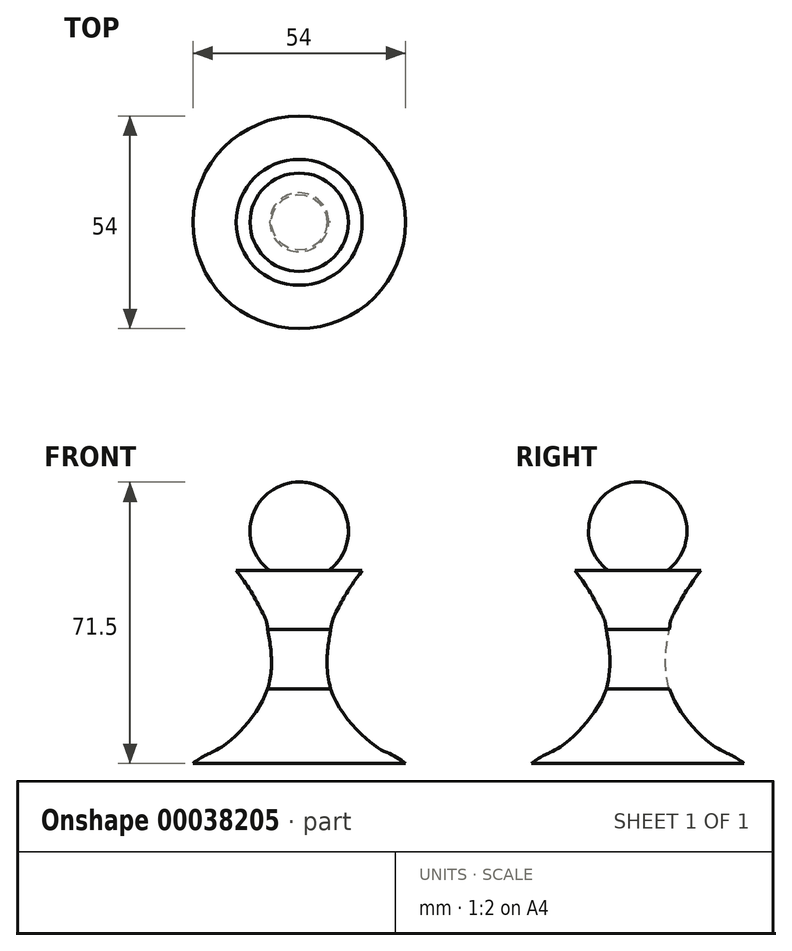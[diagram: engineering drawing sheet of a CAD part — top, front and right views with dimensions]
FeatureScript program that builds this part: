
annotation { "Feature Type Name" : "Feature", "Feature Type Description" : "" }
export const myFeature = defineFeature(function(context is Context, id is Id, definition is map)
    precondition{}
    {
        {
            var Q0;
            Q0=qCreatedBy(makeId("Front.planeOp"),FACE);
            var sketch = newSketch(context, id + "F0", { "sketchPlane" : qUnion([Q0])});
            skArc(sketch, "E0", {"start": v(7.5, 17) * mm, "mid": v(11.86, 30.95) * mm, "end": v(0, 39.5) * mm});
            skLineSegment(sketch, "E1", {"start": v(0, 27) * mm, "end": v(0, 17) * mm});
            skLineSegment(sketch, "E2", {"start": v(7.5, 17) * mm, "end": v(16, 17) * mm});
            skLineSegment(sketch, "E3", {"start": v(16, 17) * mm, "end": v(7.5, 17) * mm});
            skLineSegment(sketch, "E4", {"start": v(0, 17) * mm, "end": v(0, 2) * mm});
            skLineSegment(sketch, "E5", {"start": v(8, 2) * mm, "end": v(8, -13) * mm});
            skLineSegment(sketch, "E6", {"start": v(0, -13) * mm, "end": v(0, -28) * mm});
            skLineSegment(sketch, "E7", {"start": v(0, -32) * mm, "end": v(27, -32) * mm});
            skLineSegment(sketch, "E8", {"start": v(27, -32) * mm, "end": v(0, -32) * mm});
            skLineSegment(sketch, "E9", {"start": v(0, -30) * mm, "end": v(0, -32) * mm});
            skLineSegment(sketch, "E10", {"start": v(0, -30) * mm, "end": v(0, -28) * mm});
            skFitSpline(sketch, "E11", {"points": [v(16, 17) * mm, v(12.1, 11.43) * mm, v(10.8, 9.2) * mm, v(9.27, 6.27) * mm, v(8.37, 4.17) * mm, v(8, 2) * mm, v(8, -13) * mm, v(20, -28) * mm, v(24, -30) * mm, v(27, -32) * mm], "startDerivative": vector(-41.3, -51.96) * mm, "endDerivative": vector(25.72, -19.41) * mm});
            skLineSegment(sketch, "E12", {"start": v(0, 27) * mm, "end": v(0, 39.5) * mm});
            skLineSegment(sketch, "E13", {"start": v(0, 2) * mm, "end": v(0, -13) * mm});
            skSolve(sketch);
        }
        {
            var Q0;
            Q0=makeQuery(id+"F0.imprint","IMPRINT",FACE,{"disambiguationData":[TD([[makeQuery(id+"F0.imprint","IMPRINT",EDGE,{"derivedFrom":sQuery(id+"F0.wireOp",EDGE,"E0")}),1.0]])]});
            var Q1;
            Q1=sQuery(id+"F0.wireOp",EDGE,"E4");
            revolve(context, id + "F1", {"entities" : qUnion([Q0]), "axis" : qUnion([Q1]), "revolveType" : RevolveType.FULL});
        }
    });
